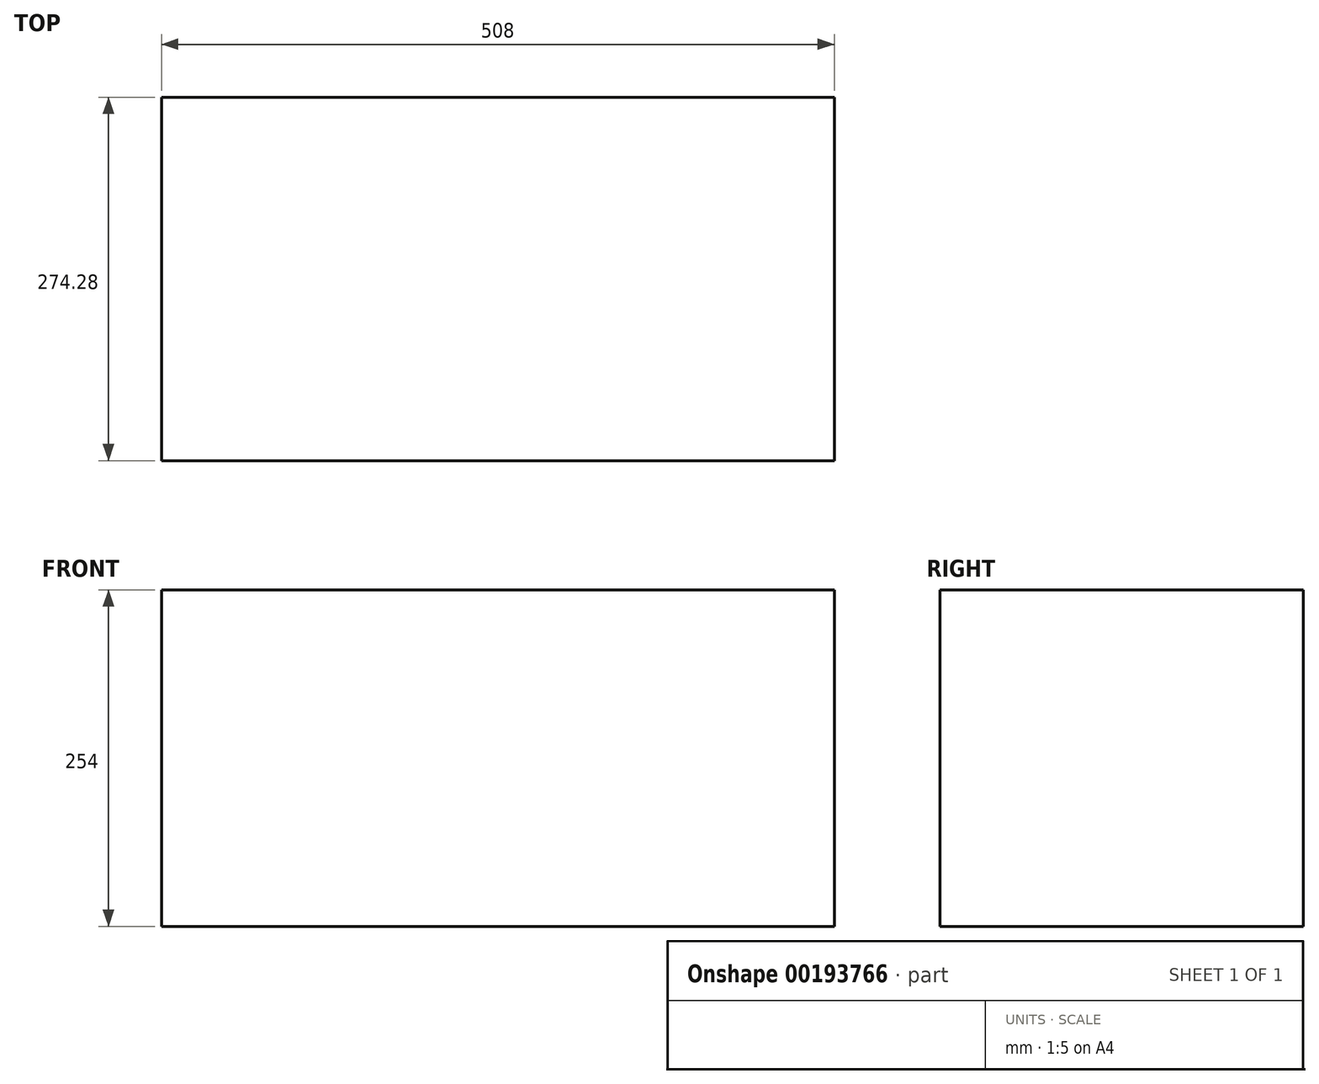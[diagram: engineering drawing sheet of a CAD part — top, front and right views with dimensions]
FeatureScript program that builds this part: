
annotation { "Feature Type Name" : "Feature", "Feature Type Description" : "" }
export const myFeature = defineFeature(function(context is Context, id is Id, definition is map)
    precondition{}
    {
        {
            var Q0;
            Q0=qCreatedBy(makeId("Top.planeOp"),FACE);
            var sketch = newSketch(context, id + "F0", { "sketchPlane" : qUnion([Q0])});
            skLineSegment(sketch, "E0.bottom", {"start": v(-254, 137.14) * mm, "end": v(254, 137.14) * mm});
            skLineSegment(sketch, "E0.top", {"start": v(-254, -137.14) * mm, "end": v(254, -137.14) * mm});
            skLineSegment(sketch, "E0.left", {"start": v(-254, 137.14) * mm, "end": v(-254, -137.14) * mm});
            skLineSegment(sketch, "E0.right", {"start": v(254, 137.14) * mm, "end": v(254, -137.14) * mm});
            skPoint(sketch, "E0.middle", {"position": v(0, 0) * mm});
            skSolve(sketch);
        }
        {
            var Q0;
            Q0=makeQuery(id+"F0.imprint","IMPRINT",FACE,{"disambiguationData":[TD([[makeQuery(id+"F0.imprint","IMPRINT",EDGE,{"derivedFrom":sQuery(id+"F0.wireOp",EDGE,"E0.bottom")}),-1.0]])]});
            extrude(context, id + "F1", {"entities" : qUnion([Q0]), "depth" : 254 * mm});
        }
    });
